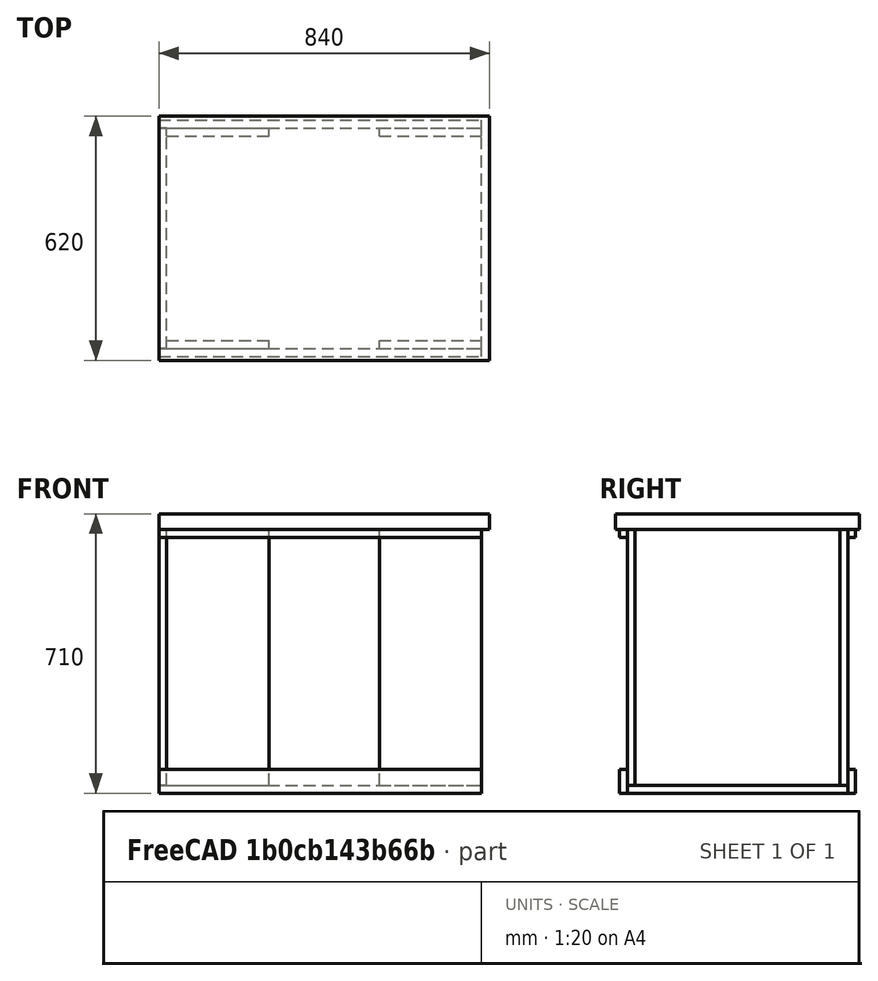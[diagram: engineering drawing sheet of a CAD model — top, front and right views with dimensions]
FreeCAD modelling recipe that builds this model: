
FCSTD DOCUMENT  (FreeCAD 0.19R24291 (Git))
Label: 3D Printer stand
License: All rights reserved
LicenseURL: http://en.wikipedia.org/wiki/All_rights_reserved
objects: Part::Box×11
note: 11 computed .brp shape members not serialized (recipe doc carries the construction recipe); baked Part::Feature solids carry a one-line shape summary decoded from their .brp

FEATURE [Part::Box] Box  label="Top"
  AttacherType = Attacher::AttachEngine3D
  Height = 40
  Length = 840
  Placement = pos=(0,0,760) rot=(0,0,1;0rad)
  Width = 620
FEATURE [Part::Box] Box001  label="Rear"
  AttacherType = Attacher::AttachEngine3D
  Height = 20
  Length = 650
  Placement = pos=(20,30,110) rot=(0,-1,0;1.5708rad)
  Width = 560
FEATURE [Part::Box] Box002  label="Bottom"
  AttacherType = Attacher::AttachEngine3D
  Height = 20
  Length = 820
  Placement = pos=(0,30,90) rot=(0,0,1;0rad)
  Width = 560
FEATURE [Part::Box] Box003  label="Side RL"
  AttacherType = Attacher::AttachEngine3D
  Height = 650
  Length = 260
  Placement = pos=(20,30,110) rot=(0,1,0;0rad)
  Width = 20
FEATURE [Part::Box] Box004  label="Side RR"
  AttacherType = Attacher::AttachEngine3D
  Height = 650
  Length = 260
  Placement = pos=(20,570,110) rot=(0,1,0;0rad)
  Width = 20
FEATURE [Part::Box] Box005  label="Side FL"
  AttacherType = Attacher::AttachEngine3D
  Height = 650
  Length = 260
  Placement = pos=(560,30,110) rot=(0,1,0;0rad)
  Width = 20
FEATURE [Part::Box] Box006  label="Side FR"
  AttacherType = Attacher::AttachEngine3D
  Height = 650
  Length = 260
  Placement = pos=(560,570,110) rot=(0,1,0;0rad)
  Width = 20
FEATURE [Part::Box] Box007  label="Plinth L"
  AttacherType = Attacher::AttachEngine3D
  Height = 60
  Length = 820
  Placement = pos=(0,10,90) rot=(0,0,1;0rad)
  Width = 20
FEATURE [Part::Box] Box008  label="Plinth R"
  AttacherType = Attacher::AttachEngine3D
  Height = 60
  Length = 820
  Placement = pos=(0,590,90) rot=(0,0,1;0rad)
  Width = 20
FEATURE [Part::Box] Box009  label="Fixing L"
  AttacherType = Attacher::AttachEngine3D
  Height = 20
  Length = 820
  Placement = pos=(0,10,740) rot=(0,0,1;0rad)
  Width = 20
FEATURE [Part::Box] Box010  label="Fixing R"
  AttacherType = Attacher::AttachEngine3D
  Height = 20
  Length = 820
  Placement = pos=(0,590,740) rot=(0,0,1;0rad)
  Width = 20
